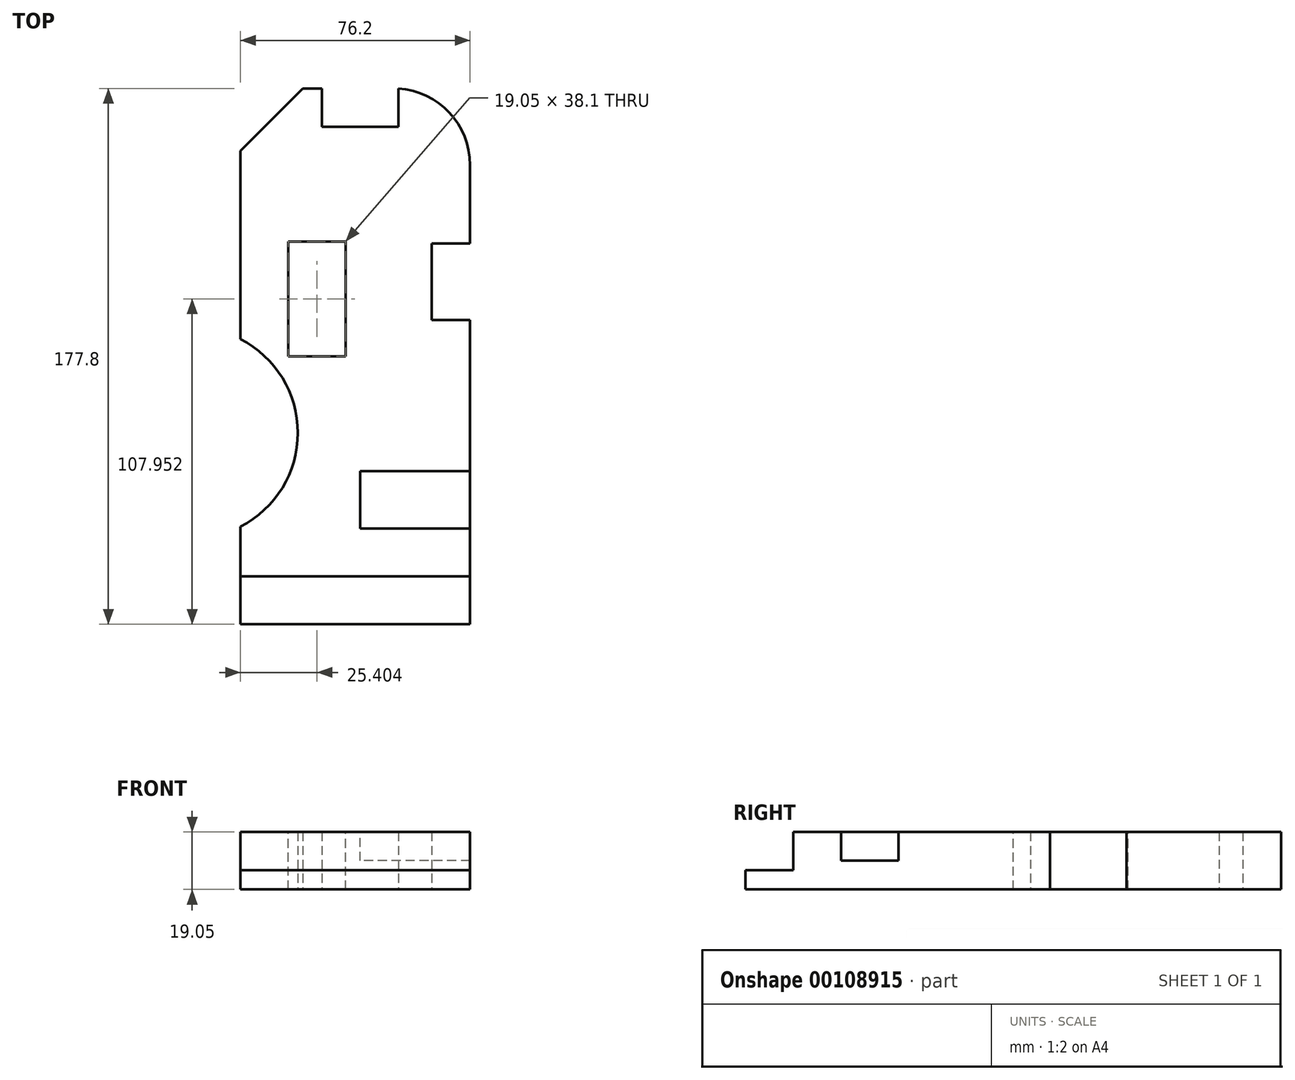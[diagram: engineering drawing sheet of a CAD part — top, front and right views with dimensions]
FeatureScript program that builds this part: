
annotation { "Feature Type Name" : "Feature", "Feature Type Description" : "" }
export const myFeature = defineFeature(function(context is Context, id is Id, definition is map)
    precondition{}
    {
        {
            var Q0;
            Q0=qCreatedBy(makeId("Top.planeOp"),FACE);
            var sketch = newSketch(context, id + "F0", { "sketchPlane" : qUnion([Q0])});
            skLineSegment(sketch, "E0.bottom", {"start": v(-39.03, -72.48) * mm, "end": v(37.17, -72.48) * mm});
            skLineSegment(sketch, "E0.top", {"start": v(-18.39, 105.32) * mm, "end": v(-12.04, 105.32) * mm});
            skLineSegment(sketch, "E0.left", {"start": v(-39.03, -72.48) * mm, "end": v(-39.03, -40.09) * mm});
            skLineSegment(sketch, "E0.right", {"start": v(37.17, -72.48) * mm, "end": v(37.17, 28.55) * mm});
            skLineSegment(sketch, "E1", {"start": v(37.17, 28.55) * mm, "end": v(24.47, 28.55) * mm});
            skLineSegment(sketch, "E2", {"start": v(24.47, 28.55) * mm, "end": v(24.47, 53.95) * mm});
            skLineSegment(sketch, "E3", {"start": v(24.47, 53.95) * mm, "end": v(37.17, 53.95) * mm});
            skLineSegment(sketch, "E4", {"start": v(-12.04, 105.32) * mm, "end": v(-12.04, 92.62) * mm});
            skLineSegment(sketch, "E5", {"start": v(-12.04, 92.62) * mm, "end": v(13.36, 92.62) * mm});
            skLineSegment(sketch, "E6", {"start": v(13.36, 92.62) * mm, "end": v(13.36, 105.32) * mm});
            skLineSegment(sketch, "E7", {"start": v(-18.39, 105.32) * mm, "end": v(-39.03, 84.68) * mm});
            skLineSegment(sketch, "E8", {"start": v(-39.03, -56.6) * mm, "end": v(-88.34, -56.6) * mm});
            skLineSegment(sketch, "E9", {"start": v(-39.03, -40.73) * mm, "end": v(-54.9, -40.73) * mm});
            skLineSegment(sketch, "E10", {"start": v(-54.9, -40.73) * mm, "end": v(-54.9, -8.98) * mm});
            skArc(sketch, "E11", {"start": v(-39.03, -40.09) * mm, "mid": v(-19.98, -8.98) * mm, "end": v(-39.03, 22.13) * mm});
            skPoint(sketch, "E12", {"position": v(-19.98, -8.98) * mm});
            skPoint(sketch, "E13.orphan", {"position": v(-39.03, 105.32) * mm});
            skLineSegment(sketch, "E14.trimOffspring", {"start": v(-39.03, 22.13) * mm, "end": v(-39.03, 84.68) * mm});
            skLineSegment(sketch, "E15.trimOffspring", {"start": v(37.17, 53.95) * mm, "end": v(37.17, 105.32) * mm});
            skLineSegment(sketch, "E16.trimOffspring", {"start": v(13.36, 105.32) * mm, "end": v(37.17, 105.32) * mm});
            skSolve(sketch);
        }
        {
            var Q0;
            Q0 = qSketchRegion(id + "F0", true);
            extrude(context, id + "F1", {"entities" : qUnion([Q0]), "depth" : 19.05 * mm});
        }
        {
            var Q0;
            Q0=makeQuery(id+"F1.opExtrude","CAP_FACE",FACE,{"disambiguationData":[OSD([sQuery(id+"F0.wireOp",EDGE,"E0.bottom"),sQuery(id+"F0.wireOp",EDGE,"E0.top"),sQuery(id+"F0.wireOp",EDGE,"E0.left"),sQuery(id+"F0.wireOp",EDGE,"E0.right"),sQuery(id+"F0.wireOp",EDGE,"E1"),sQuery(id+"F0.wireOp",EDGE,"E2"),sQuery(id+"F0.wireOp",EDGE,"E3"),sQuery(id+"F0.wireOp",EDGE,"E4"),sQuery(id+"F0.wireOp",EDGE,"E5"),sQuery(id+"F0.wireOp",EDGE,"E6"),sQuery(id+"F0.wireOp",EDGE,"E7"),sQuery(id+"F0.wireOp",EDGE,"E9"),sQuery(id+"F0.wireOp",EDGE,"E11"),sQuery(id+"F0.wireOp",EDGE,"E14.trimOffspring"),sQuery(id+"F0.wireOp",EDGE,"E15.trimOffspring"),sQuery(id+"F0.wireOp",EDGE,"E16.trimOffspring")])],"isStart":false});
            var sketch = newSketch(context, id + "F2", { "sketchPlane" : qUnion([Q0])});
            skLineSegment(sketch, "E17.bottom", {"start": v(-39.03, -56.6) * mm, "end": v(37.17, -56.6) * mm});
            skLineSegment(sketch, "E17.top", {"start": v(-39.03, -72.48) * mm, "end": v(37.17, -72.48) * mm});
            skLineSegment(sketch, "E17.left", {"start": v(-39.03, -56.6) * mm, "end": v(-39.03, -72.48) * mm});
            skLineSegment(sketch, "E17.right", {"start": v(37.17, -56.6) * mm, "end": v(37.17, -72.48) * mm});
            skSolve(sketch);
        }
        {
            var Q0;
            Q0 = qSketchRegion(id + "F2", true);
            extrude(context, id + "F3", {"entities" : qUnion([Q0]), "operationType" : NewBodyOperationType.REMOVE, "oppositeDirection" : true, "depth" : 12.7 * mm});
        }
        {
            var Q0;
            Q0=makeQuery(id+"F1.opExtrude","CAP_FACE",FACE,{"disambiguationData":[OSD([sQuery(id+"F0.wireOp",EDGE,"E0.bottom"),sQuery(id+"F0.wireOp",EDGE,"E0.top"),sQuery(id+"F0.wireOp",EDGE,"E0.left"),sQuery(id+"F0.wireOp",EDGE,"E0.right"),sQuery(id+"F0.wireOp",EDGE,"E1"),sQuery(id+"F0.wireOp",EDGE,"E2"),sQuery(id+"F0.wireOp",EDGE,"E3"),sQuery(id+"F0.wireOp",EDGE,"E4"),sQuery(id+"F0.wireOp",EDGE,"E5"),sQuery(id+"F0.wireOp",EDGE,"E6"),sQuery(id+"F0.wireOp",EDGE,"E7"),sQuery(id+"F0.wireOp",EDGE,"E11"),sQuery(id+"F0.wireOp",EDGE,"E14.trimOffspring"),sQuery(id+"F0.wireOp",EDGE,"E15.trimOffspring"),sQuery(id+"F0.wireOp",EDGE,"E16.trimOffspring")])],"isStart":false});
            var sketch = newSketch(context, id + "F4", { "sketchPlane" : qUnion([Q0])});
            skLineSegment(sketch, "E18.bottom", {"start": v(37.17, -21.68) * mm, "end": v(0.66, -21.68) * mm});
            skLineSegment(sketch, "E18.top", {"start": v(37.17, -40.73) * mm, "end": v(0.66, -40.73) * mm});
            skLineSegment(sketch, "E18.left", {"start": v(37.17, -21.68) * mm, "end": v(37.17, -40.73) * mm});
            skLineSegment(sketch, "E18.right", {"start": v(0.66, -21.68) * mm, "end": v(0.66, -40.73) * mm});
            skSolve(sketch);
        }
        {
            var Q0;
            Q0 = qSketchRegion(id + "F4", true);
            extrude(context, id + "F5", {"entities" : qUnion([Q0]), "operationType" : NewBodyOperationType.REMOVE, "oppositeDirection" : true, "depth" : 9.52 * mm});
        }
        {
            var Q0;
            Q0=makeQuery(id+"F1.opExtrude","CAP_FACE",FACE,{"disambiguationData":[OSD([sQuery(id+"F0.wireOp",EDGE,"E0.bottom"),sQuery(id+"F0.wireOp",EDGE,"E0.top"),sQuery(id+"F0.wireOp",EDGE,"E0.left"),sQuery(id+"F0.wireOp",EDGE,"E0.right"),sQuery(id+"F0.wireOp",EDGE,"E1"),sQuery(id+"F0.wireOp",EDGE,"E2"),sQuery(id+"F0.wireOp",EDGE,"E3"),sQuery(id+"F0.wireOp",EDGE,"E4"),sQuery(id+"F0.wireOp",EDGE,"E5"),sQuery(id+"F0.wireOp",EDGE,"E6"),sQuery(id+"F0.wireOp",EDGE,"E7"),sQuery(id+"F0.wireOp",EDGE,"E11"),sQuery(id+"F0.wireOp",EDGE,"E14.trimOffspring"),sQuery(id+"F0.wireOp",EDGE,"E15.trimOffspring"),sQuery(id+"F0.wireOp",EDGE,"E16.trimOffspring")])],"isStart":false});
            var sketch = newSketch(context, id + "F6", { "sketchPlane" : qUnion([Q0])});
            skLineSegment(sketch, "E19.bottom", {"start": v(-23.15, 54.52) * mm, "end": v(-4.1, 54.52) * mm});
            skLineSegment(sketch, "E19.top", {"start": v(-23.15, 16.42) * mm, "end": v(-4.1, 16.42) * mm});
            skLineSegment(sketch, "E19.left", {"start": v(-23.15, 54.52) * mm, "end": v(-23.15, 16.42) * mm});
            skLineSegment(sketch, "E19.right", {"start": v(-4.1, 54.52) * mm, "end": v(-4.1, 16.42) * mm});
            skSolve(sketch);
        }
        {
            var Q0;
            Q0 = qSketchRegion(id + "F6", true);
            extrude(context, id + "F7", {"entities" : qUnion([Q0]), "operationType" : NewBodyOperationType.REMOVE, "oppositeDirection" : true, "depth" : 25.4 * mm});
        }
        {
            var Q0;
            Q0=makeQuery(id+"F1.opExtrude","SWEPT_EDGE",EDGE,{"disambiguationData":[OSD([sQuery(id+"F0.wireOp",EDGE,"E15.trimOffspring"),sQuery(id+"F0.wireOp",EDGE,"E16.trimOffspring")])]});
            fillet(context, id + "F8", {"entities" : qUnion([Q0]), "radius" : 25.4 * mm, "tangentPropagation" : true, "allowEdgeOverflow" : false});
        }
    });
